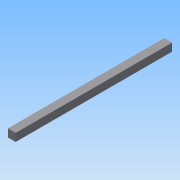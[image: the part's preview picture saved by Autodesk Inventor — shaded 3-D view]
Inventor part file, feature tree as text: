
AUTODESK INVENTOR PART (.ipt)
format: ipt  version: 2015 (Build 190159000, 159)  size: 67,072 bytes
history: native  units: mm
features: extrude x1, sketch x1
ambient origin geometry x8: Origin, YZ Plane, XZ Plane, XY Plane, X Axis, Y Axis, Z Axis, Center Point
bodies: Solid1 (feature_tree)
feature tree (2):
  extrude  "Extrusion1"  Depth=10.0mm
  sketch  "Sketch1"  dims[d0=10.0mm d1=10.0mm d2=200.0mm d3=0.0mm]
